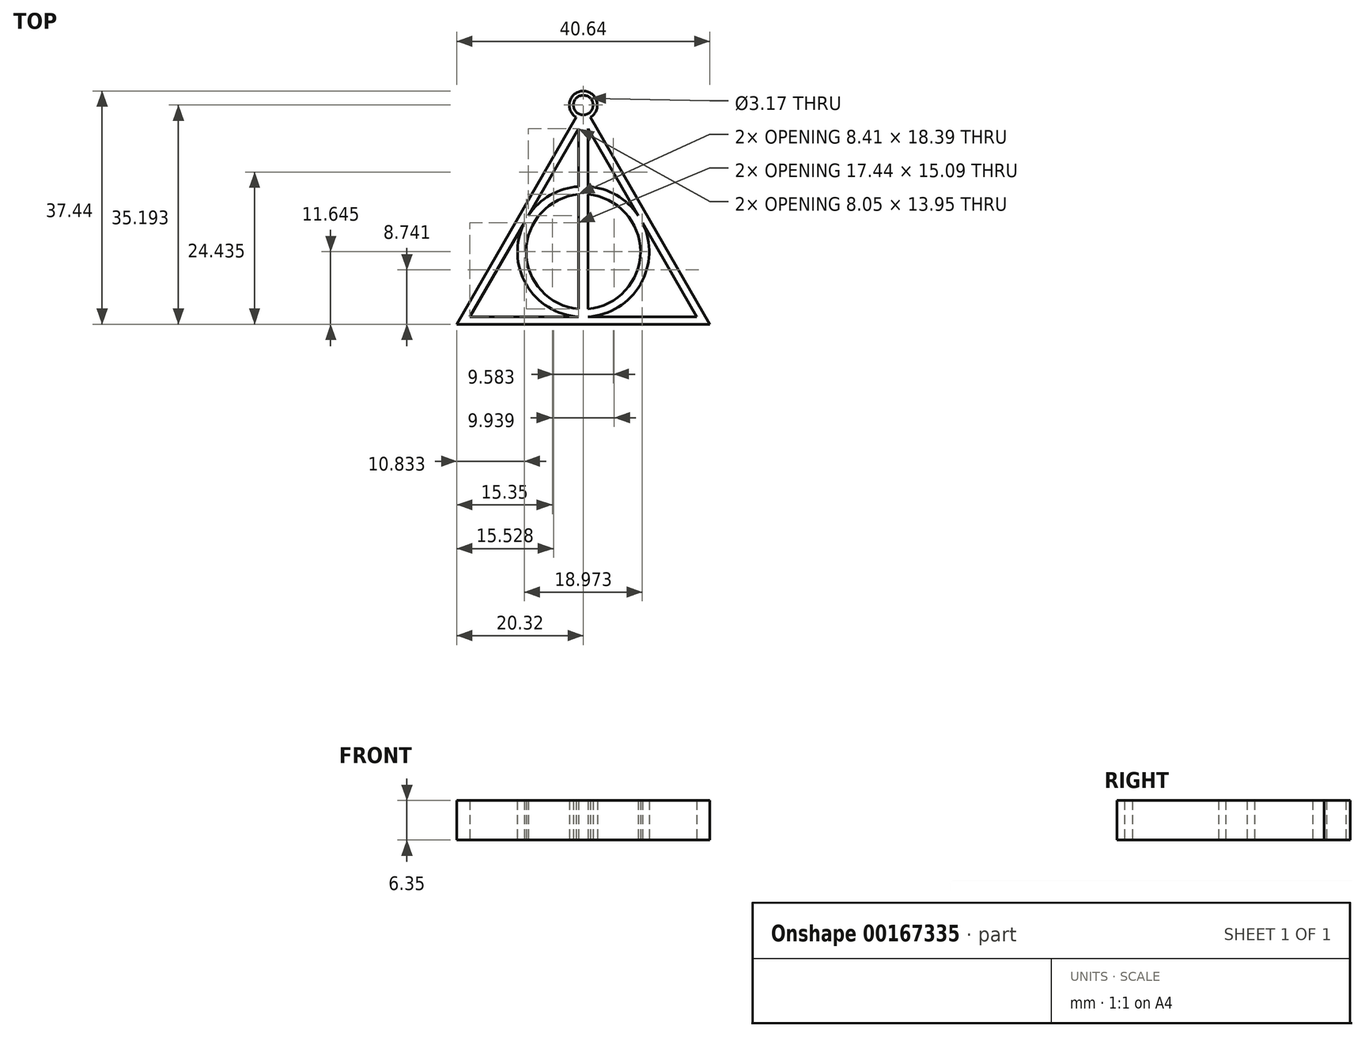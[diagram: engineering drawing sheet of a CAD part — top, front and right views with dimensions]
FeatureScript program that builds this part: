
annotation { "Feature Type Name" : "Feature", "Feature Type Description" : "" }
export const myFeature = defineFeature(function(context is Context, id is Id, definition is map)
    precondition{}
    {
        {
            var Q0;
            Q0=qCreatedBy(makeId("Top.planeOp"),FACE);
            var sketch = newSketch(context, id + "F0", { "sketchPlane" : qUnion([Q0])});
            skLineSegment(sketch, "E0", {"start": v(-20.32, -10.3) * mm, "end": v(0, -10.3) * mm});
            skLineSegment(sketch, "E1", {"start": v(-18.2, -9.1) * mm, "end": v(-9.5, 5.99) * mm});
            skLineSegment(sketch, "E2", {"start": v(-18.2, -9.1) * mm, "end": v(-0.76, -9.1) * mm});
            skLineSegment(sketch, "E3", {"start": v(-0.76, -7.85) * mm, "end": v(-0.76, 10.54) * mm});
            skArc(sketch, "E4", {"start": v(-0.76, 11.8) * mm, "mid": v(-5.33, 10.42) * mm, "end": v(-8.82, 7.16) * mm});
            skArc(sketch, "E5", {"start": v(-0.76, 10.54) * mm, "mid": v(-9.17, 1.35) * mm, "end": v(-0.76, -7.85) * mm});
            skArc(sketch, "E6.trimOffspring", {"start": v(-9.5, 5.99) * mm, "mid": v(-9.17, -3.9) * mm, "end": v(-0.76, -9.1) * mm});
            skLineSegment(sketch, "E7.trimOffspring", {"start": v(-8.82, 7.16) * mm, "end": v(-0.76, 21.1) * mm});
            skLineSegment(sketch, "E8.trimOffspring", {"start": v(-0.76, 11.8) * mm, "end": v(-0.76, 21.1) * mm});
            skLineSegment(sketch, "E9.MirrorCS", {"start": v(0.76, 11.8) * mm, "end": v(0.76, 21.1) * mm});
            skLineSegment(sketch, "E10.MirrorCS", {"start": v(8.82, 7.16) * mm, "end": v(0.76, 21.1) * mm});
            skArc(sketch, "E11.MirrorCS", {"start": v(9.5, 5.99) * mm, "mid": v(9.17, -3.9) * mm, "end": v(0.76, -9.1) * mm});
            skArc(sketch, "E12.MirrorCS", {"start": v(0.76, 10.54) * mm, "mid": v(9.17, 1.35) * mm, "end": v(0.76, -7.85) * mm});
            skArc(sketch, "E13.MirrorCS", {"start": v(0.76, 11.8) * mm, "mid": v(5.33, 10.42) * mm, "end": v(8.82, 7.16) * mm});
            skLineSegment(sketch, "E14.MirrorCS", {"start": v(0.76, -7.85) * mm, "end": v(0.76, 10.54) * mm});
            skLineSegment(sketch, "E15.MirrorCS", {"start": v(18.2, -9.1) * mm, "end": v(0.76, -9.1) * mm});
            skLineSegment(sketch, "E16.MirrorCS", {"start": v(18.2, -9.1) * mm, "end": v(9.5, 5.99) * mm});
            skLineSegment(sketch, "E17.MirrorCS", {"start": v(20.32, -10.3) * mm, "end": v(0, -10.3) * mm});
            skPoint(sketch, "E18.oppositeSnap0", {"position": v(0, 25.6) * mm});
            skArc(sketch, "E19", {"start": v(1.13, 22.94) * mm, "mid": v(0, 27.14) * mm, "end": v(-1.13, 22.94) * mm});
            skArc(sketch, "E20", {"start": v(0.8, 23.52) * mm, "mid": v(0, 26.48) * mm, "end": v(-0.8, 23.52) * mm});
            skLineSegment(sketch, "E21.trimOffspring", {"start": v(-1.13, 22.94) * mm, "end": v(-20.32, -10.3) * mm});
            skLineSegment(sketch, "E22.trimOffspring", {"start": v(1.13, 22.94) * mm, "end": v(20.32, -10.3) * mm});
            skCircle(sketch, "E23", {"center": v(0, 24.9) * mm, "radius": 1.58 * mm});
            skSolve(sketch);
        }
        {
            var Q0;
            Q0=makeQuery(id+"F0.imprint","IMPRINT",FACE,{"disambiguationData":[TD([[makeQuery(id+"F0.imprint","IMPRINT",EDGE,{"derivedFrom":sQuery(id+"F0.wireOp",EDGE,"E0")}),1.0]])]});
            extrude(context, id + "F1", {"entities" : qUnion([Q0]), "depth" : 6.35 * mm});
        }
    });
